# Revit family: QF_BOURGEAT_Bourgeat_Socles_Rouleurs
name_source: partatom
category: Equipement spécialisé
revit_build: Autodesk Revit 2015 (Build: 20140606_1530(x64)
units: mm (PartAtom-declared; Revit-internal decimal feet)

## types (5) — shared parameters
Certification = NF hygiene alimentaire
Fabricant = BOURGEAT
Spécification du Fabricant = Socles Rouleurs
URL catalogue = http://www.bourgeat.fr

## per-type parameters (varying)
| type | Barre renfort | Barreaux | Cadre Universel | Charge max | Décalage RAr X | Décalage RAr Y | Décalage RAv X | Décalage RAv Y | Epaisseur poignées sur cadre | Hauteur hors tout | Largeur Plateau | Longueur hors tout | Longueur plateau | Modèle | Plateau Rond | Plateau plein carrée | Poids net à vide | Poignées sur cadre | Poignées sur roulettes | Profondeur hors tout |
| Modèle pour casiers | 545 mm | Non | Non | 50.00 kg | 140 mm  [stored 0.459318 ft] | 50 mm  [stored 0.164042 ft] | 50 mm  [stored 0.164042 ft] | 50 mm  [stored 0.164042 ft] | 128 mm | 1050 mm | 505 mm  [stored 1.65682 ft] | 670 mm  [stored 2.19816 ft] | 505 mm  [stored 1.65682 ft] | 797106 | Non | Oui | 7.50 kg | Oui | Non | 580 mm  [stored 1.90289 ft] |
| Modèle pour conteneurs | 755 mm  [stored 2.47703 ft] | Oui | Non | 120.00 kg | 110 mm  [stored 0.360892 ft] | 50 mm  [stored 0.164042 ft] | 50 mm  [stored 0.164042 ft] | 50 mm  [stored 0.164042 ft] | 98 mm | 1050 mm | 540 mm  [stored 1.77165 ft] | 880 mm  [stored 2.88714 ft] | 745 mm  [stored 2.44423 ft] | 797606 | Non | Non | 8.40 kg | Oui | Non | 615 mm  [stored 2.01772 ft] |
| Modèle renforcé pour casiers | 636 mm  [stored 2.08661 ft] | Non | Non | 80.00 kg | 78 mm | 50 mm  [stored 0.164042 ft] | 50 mm  [stored 0.164042 ft] | 50 mm  [stored 0.164042 ft] | 128 mm | 1050 mm | 559 mm  [stored 1.83399 ft] | 761 mm  [stored 2.49672 ft] | 658 mm | 797306 | Non | Non | 9.00 kg | Non | Oui | 634 mm  [stored 2.08005 ft] |
| Modèle "universel" | 620 mm  [stored 2.03412 ft] | Non | Oui | 120.00 kg | 50 mm  [stored 0.164042 ft] | 113 mm | 50 mm  [stored 0.164042 ft] | 50 mm  [stored 0.164042 ft] | 128 mm | 1010 mm  [stored 3.31365 ft] | 505 mm  [stored 1.65682 ft] | 745 mm  [stored 2.44423 ft] | 580 mm  [stored 1.90289 ft] | 798106 | Non | Non | 11.50 kg | Non | Non | 580 mm  [stored 1.90289 ft] |
| Modèle pour marmites | 330 mm | Non | Non | 40.00 kg | 105 mm  [stored 0.344488 ft] | 105 mm  [stored 0.344488 ft] | 105 mm  [stored 0.344488 ft] | 105 mm  [stored 0.344488 ft] | 128 mm | 195 mm  [stored 0.639764 ft] | 380 mm  [stored 1.24672 ft] | 455 mm  [stored 1.49278 ft] | 290 mm | 797806 | Oui | Non | 4.90 kg | Non | Non | 455 mm  [stored 1.49278 ft] |

note: [stored X ft] marks values corroborated as IEEE doubles in the binary element streams (Revit-internal decimal feet)
